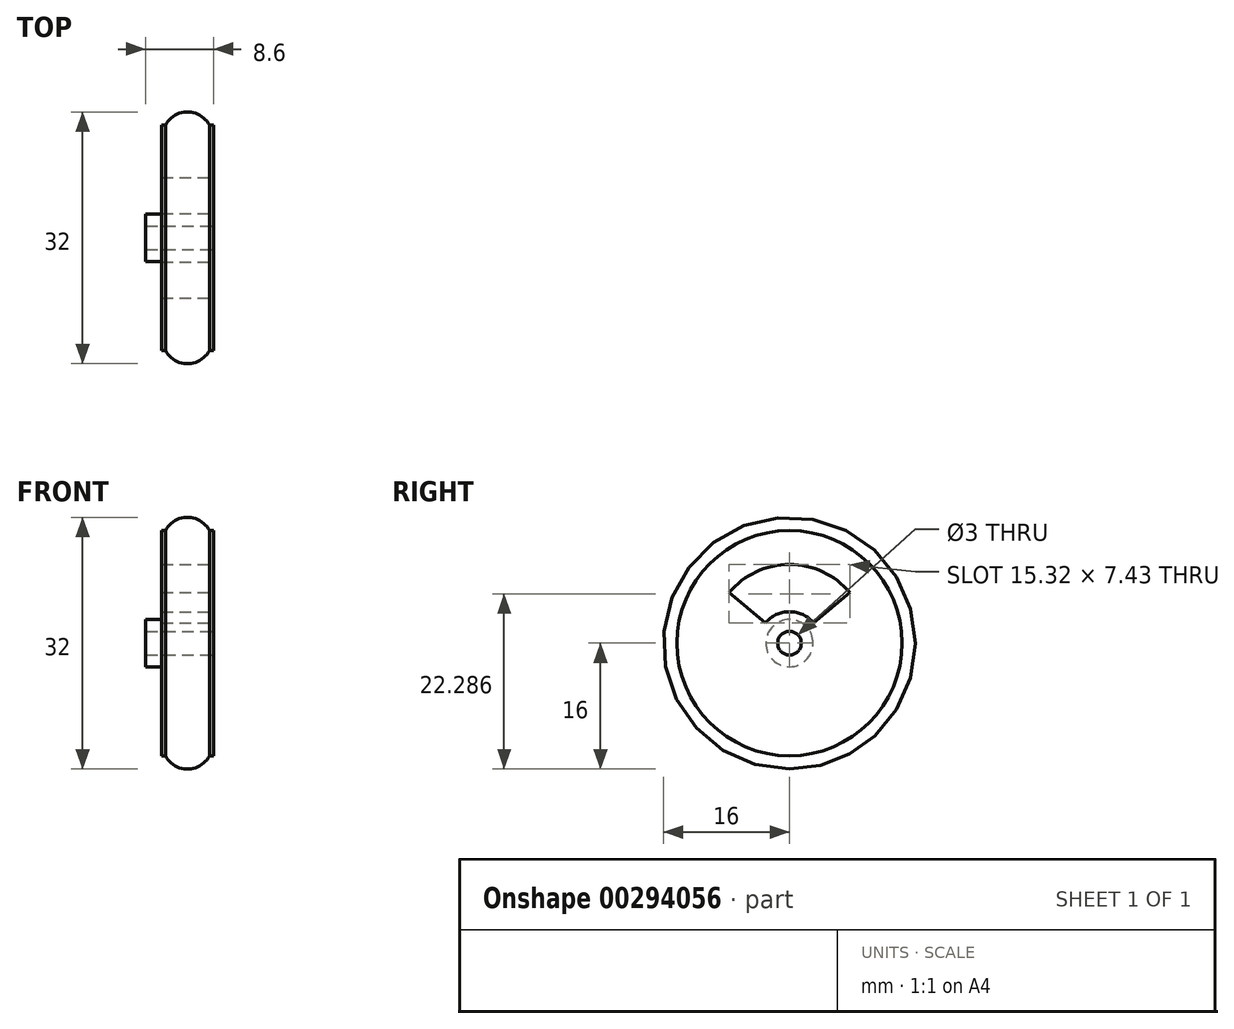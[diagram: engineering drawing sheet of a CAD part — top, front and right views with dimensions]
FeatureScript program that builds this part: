
annotation { "Feature Type Name" : "Feature", "Feature Type Description" : "" }
export const myFeature = defineFeature(function(context is Context, id is Id, definition is map)
    precondition{}
    {
        {
            var Q0;
            Q0=qCreatedBy(makeId("Top.planeOp"),FACE);
            var sketch = newSketch(context, id + "F0", { "sketchPlane" : qUnion([Q0])});
            skLineSegment(sketch, "E0", {"start": v(0, 0) * mm, "end": v(0, 3) * mm});
            skLineSegment(sketch, "E1", {"start": v(0, 3) * mm, "end": v(2, 3) * mm});
            skLineSegment(sketch, "E2", {"start": v(2, 3) * mm, "end": v(2, 14.3) * mm});
            skLineSegment(sketch, "E3", {"start": v(2, 14.3) * mm, "end": v(2.5, 14.3) * mm});
            skLineSegment(sketch, "E4", {"start": v(8.1, 14.3) * mm, "end": v(8.6, 14.3) * mm});
            skLineSegment(sketch, "E5", {"start": v(8.6, 14.3) * mm, "end": v(8.6, 0) * mm});
            skLineSegment(sketch, "E6", {"start": v(8.6, 0) * mm, "end": v(0, 0) * mm});
            skPoint(sketch, "E7.startSnap0", {"position": v(5.3, 16) * mm});
            skLineSegment(sketch, "E8", {"start": v(4.76, 14.3) * mm, "end": v(2.5, 14.3) * mm, "construction": true});
            skArc(sketch, "E9", {"start": v(8.1, 14.3) * mm, "mid": v(5.3, 16) * mm, "end": v(2.5, 14.3) * mm});
            skLineSegment(sketch, "E10", {"start": v(5.3, 16) * mm, "end": v(5.3, 12.84) * mm, "construction": true});
            skSolve(sketch);
        }
        {
            var Q0;
            Q0=makeQuery(id+"F0.imprint","IMPRINT",FACE,{"disambiguationData":[TD([[makeQuery(id+"F0.imprint","IMPRINT",EDGE,{"derivedFrom":sQuery(id+"F0.wireOp",EDGE,"E0")}),-1.0]])]});
            var Q1;
            Q1=sQuery(id+"F0.wireOp",EDGE,"E6");
            revolve(context, id + "F1", {"entities" : qUnion([Q0]), "axis" : qUnion([Q1]), "revolveType" : RevolveType.FULL});
        }
        {
            var Q0;
            Q0=makeQuery(id+"F1.opRevolve","SWEPT_FACE",FACE,{"disambiguationData":[OSD([sQuery(id+"F0.wireOp",EDGE,"E5")])]});
            var sketch = newSketch(context, id + "F2", { "sketchPlane" : qUnion([Q0])});
            skCircle(sketch, "E11", {"center": v(0, 0) * mm, "radius": 1.5 * mm});
            skLineSegment(sketch, "E12", {"start": v(0, 0) * mm, "end": v(0, 7.34) * mm, "construction": true});
            skLineSegment(sketch, "E13", {"start": v(0, 0) * mm, "end": v(3.06, 2.57) * mm, "construction": true});
            skLineSegment(sketch, "E14", {"start": v(3.06, 2.57) * mm, "end": v(7.66, 6.43) * mm});
            skArc(sketch, "E15", {"start": v(7.66, 6.43) * mm, "mid": v(0, 10) * mm, "end": v(-7.66, 6.43) * mm});
            skLineSegment(sketch, "E16.MirrorCS", {"start": v(-3.06, 2.57) * mm, "end": v(-7.66, 6.43) * mm});
            skArc(sketch, "E17", {"start": v(3.06, 2.57) * mm, "mid": v(0, 4) * mm, "end": v(-3.06, 2.57) * mm});
            skSolve(sketch);
        }
        {
            var Q0;
            Q0 = qSketchRegion(id + "F2", true);
            extrude(context, id + "F3", {"entities" : qUnion([Q0]), "operationType" : NewBodyOperationType.REMOVE, "oppositeDirection" : true, "depth" : 25 * mm});
        }
    });
